# Revit family: Lighting_Outside_Focus-Lighting_Space
name_source: partatom
category: Lighting Fixtures
revit_build: Autodesk Revit 2017 (Build: 20190508_0315(x64)
units: mm (PartAtom-declared; Revit-internal decimal feet)

## family parameters
Always vertical = Yes
Cut with Voids When Loaded = No
Light Source = Yes
OmniClass Number = 23.80.70.14.21
OmniClass Title = Street and Roadway Lighting
Part Type = Normal
Room Calculation Point = No
Round Connector Dimension = Use Diameter
Shared = No
Work Plane-Based = No

## types (2) — shared parameters
AssetType = Fixed
BIMObjectName = Lighting_Outside_Focus-Lighting_Space
Brand = Focus Lighting
Category = Street/Urban
Color = Various
Color Filter = 16777215
Dimming Lamp Color Temperature Shift = <None>
DurationUnit = Hours
ExpectedLife = 100000
Features = + Comfortable direct/indirect lighting
+ Excellent light distribution with unique uniformity
+ Elegant on high and low columns
+ Easy smart city integration
+ Dark-sky friendly lighting
+ Option for asymmetrical lighting
+ Suitable for Ø 60 and 76 mm standard columns
+ Cylindrical columns Ø 90-180 mm
+ Highly corrosion resistant
Finish = Powdered aluminium
HasProtectiveEarth = Yes
IP_Code = IP66, class 2
IfcExportAs = IfcLightFixtureType
IfcExportType = NOTDEFINED
LensMaterial = Polycarbonate, Clear
LightFixtureMountingType = Surface
LightFixturePlacingType = Pole
LightFixtureSecondaryMaterial = Glass
Manufacturer = Focus Lighting
ManufacturerName = Focus Lighting
ManufacturerURL = https://www.focus-lighting.dk
Material = Aluminium, polycarbonate
NBSDescription = General purpose luminaires
NBSReference = 90-60-50/405
Name = Focus-Lighting_Space
NominalCurrent = 22 A
NominalDiameter = 640 mm  [stored 2.09974 ft]
NominalFrequencyRange = 0 Hz
NominalHeight = 4465 mm  [stored 14.649 ft]
NominalLength = 640 mm  [stored 2.09974 ft]
NominalRadius = 320 mm  [stored 1.04987 ft]
NominalVoltage = 220 V
NominalVoltageCalc = 0 V
NominalWidth = 640 mm  [stored 2.09974 ft]
NumberOfPoles = 1
PhaseAngle = 0.00°
Photometric Web File = Space.IES
ProductInformation = AART Designers and Focus Lighting have created Space, a sophisticated, large-scale luminaire with outstanding lighting properties. Circular shades and diffusers are desiged to expand the light from a compact LED to powerful and comfortable illumination - creating new human spaces.
Shape = Sculptured
Size = 640x640x4465 mm
Tilt Angle = 90.00°
TotalWattage = 60 W
Uniclass2 = Pr_80_77_48_03
Uniclass2015Description = Aluminium lighting columns
Uniclass2015Reference = Pr_80_77_48_03
UsageCurrent = 0 A
Version = 1
VersionDate = 06/04/2020
zero-valued in all types: DefaultElevation, ElectricalDeviceNominalPower, MaintenanceFactor, NumberOfSources

## per-type parameters (varying)
| type | ColumnDiameter | ConvergoRefNr |
| Space - Ø90 column | Space 90 | 0147-2003-0001-DK |
| Space - Ø60 column | Space 60 | 0147-2003-0002-DK |

note: column(s) folded — value = type name in every type: Model

note: [stored X ft] marks values corroborated as IEEE doubles in the binary element streams (Revit-internal decimal feet)

## geometry (parser evidence)
native form markers: Sweep x8
no freeform markers — native parametric forms only
